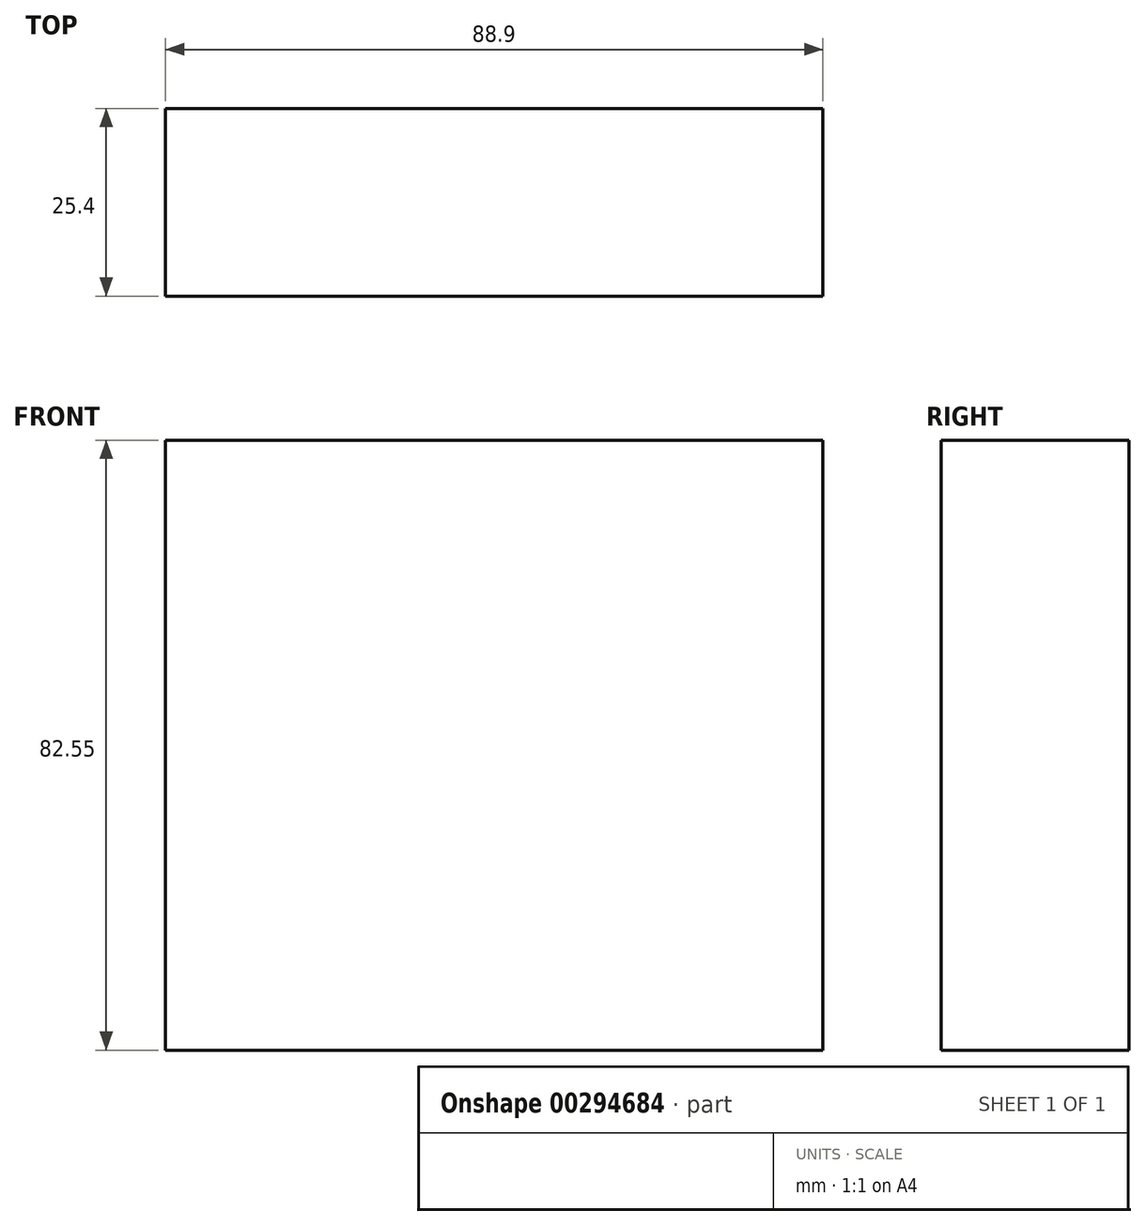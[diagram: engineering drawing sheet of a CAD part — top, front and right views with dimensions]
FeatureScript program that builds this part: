
annotation { "Feature Type Name" : "Feature", "Feature Type Description" : "" }
export const myFeature = defineFeature(function(context is Context, id is Id, definition is map)
    precondition{}
    {
        {
            var Q0;
            Q0=qCreatedBy(makeId("Front.planeOp"),FACE);
            var sketch = newSketch(context, id + "F0", { "sketchPlane" : qUnion([Q0])});
            skLineSegment(sketch, "E0.bottom", {"start": v(0, 0) * mm, "end": v(-88.9, 0) * mm});
            skLineSegment(sketch, "E0.top", {"start": v(0, 82.55) * mm, "end": v(-88.9, 82.55) * mm});
            skLineSegment(sketch, "E0.left", {"start": v(0, 0) * mm, "end": v(0, 82.55) * mm});
            skLineSegment(sketch, "E0.right", {"start": v(-88.9, 0) * mm, "end": v(-88.9, 82.55) * mm});
            skSolve(sketch);
        }
        {
            var Q0;
            Q0=makeQuery(id+"F0.imprint","IMPRINT",FACE,{"disambiguationData":[TD([[makeQuery(id+"F0.imprint","IMPRINT",EDGE,{"derivedFrom":sQuery(id+"F0.wireOp",EDGE,"E0.bottom")}),-1.0]])]});
            extrude(context, id + "F1", {"entities" : qUnion([Q0]), "depth" : 25.4 * mm});
        }
    });
